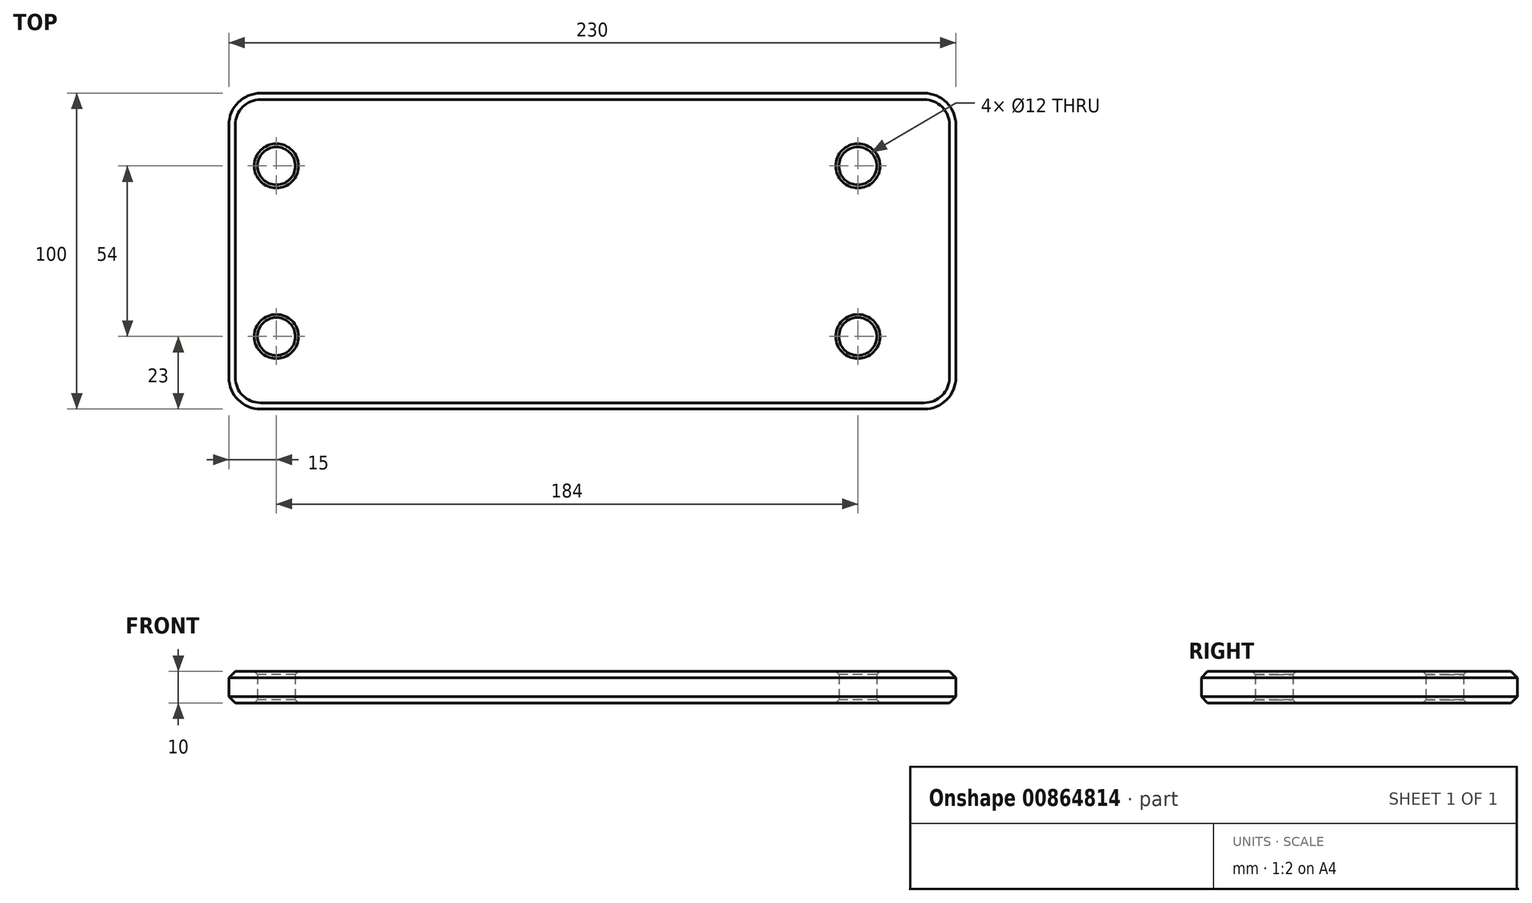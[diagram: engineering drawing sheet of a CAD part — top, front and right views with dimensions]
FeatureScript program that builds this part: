
annotation { "Feature Type Name" : "Feature", "Feature Type Description" : "" }
export const myFeature = defineFeature(function(context is Context, id is Id, definition is map)
    precondition{}
    {
        {
            var Q0;
            Q0=qCreatedBy(makeId("Top.planeOp"),FACE);
            var sketch = newSketch(context, id + "F0", { "sketchPlane" : qUnion([Q0])});
            skLineSegment(sketch, "E0.bottom", {"start": v(105, 50) * mm, "end": v(-105, 50) * mm});
            skLineSegment(sketch, "E0.top", {"start": v(105, -50) * mm, "end": v(-105, -50) * mm});
            skLineSegment(sketch, "E0.left", {"start": v(115, 40) * mm, "end": v(115, -40) * mm});
            skLineSegment(sketch, "E0.right", {"start": v(-115, 40) * mm, "end": v(-115, -40) * mm});
            skPoint(sketch, "E0.middle", {"position": v(0, 0) * mm});
            skPoint(sketch, "E1.visualSharp", {"position": v(-115, 50) * mm});
            skArc(sketch, "E1.filletArc", {"start": v(-105, 50) * mm, "mid": v(-112.07, 47.07) * mm, "end": v(-115, 40) * mm});
            skPoint(sketch, "E2.visualSharp", {"position": v(-115, -50) * mm});
            skArc(sketch, "E2.filletArc", {"start": v(-115, -40) * mm, "mid": v(-112.07, -47.07) * mm, "end": v(-105, -50) * mm});
            skPoint(sketch, "E3.visualSharp", {"position": v(115, 50) * mm});
            skArc(sketch, "E3.filletArc", {"start": v(115, 40) * mm, "mid": v(112.07, 47.07) * mm, "end": v(105, 50) * mm});
            skPoint(sketch, "E4.visualSharp", {"position": v(115, -50) * mm});
            skArc(sketch, "E4.filletArc", {"start": v(105, -50) * mm, "mid": v(112.07, -47.07) * mm, "end": v(115, -40) * mm});
            skLineSegment(sketch, "E5", {"start": v(-100, 50) * mm, "end": v(-100, -50) * mm, "construction": true});
            skLineSegment(sketch, "E6", {"start": v(-115, -27) * mm, "end": v(115, -27) * mm, "construction": true});
            skLineSegment(sketch, "E7", {"start": v(-115, 27) * mm, "end": v(115, 27) * mm, "construction": true});
            skLineSegment(sketch, "E8", {"start": v(84, 50) * mm, "end": v(84, -50) * mm, "construction": true});
            skCircle(sketch, "E9", {"center": v(-100, 27) * mm, "radius": 6 * mm});
            skCircle(sketch, "E10", {"center": v(-100, -27) * mm, "radius": 6 * mm});
            skCircle(sketch, "E11", {"center": v(84, 27) * mm, "radius": 6 * mm});
            skCircle(sketch, "E12", {"center": v(84, -27) * mm, "radius": 6 * mm});
            skSolve(sketch);
        }
        {
            var Q0;
            Q0=makeQuery(id+"F0.imprint","IMPRINT",FACE,{"disambiguationData":[TD([[makeQuery(id+"F0.imprint","IMPRINT",EDGE,{"derivedFrom":sQuery(id+"F0.wireOp",EDGE,"E0.bottom")}),1.0]])]});
            extrude(context, id + "F1", {"entities" : qUnion([Q0]), "depth" : 10 * mm, "offsetDistance" : 25 * mm});
        }
        {
            var Q0;
            Q0=makeQuery(id+"F1.opExtrude","CAP_EDGE",EDGE,{"disambiguationData":[OSD([sQuery(id+"F0.wireOp",EDGE,"E0.top")])],"isStart":false});
            chamfer(context, id + "F2", {"entities" : qUnion([Q0]), "width" : 2 * mm, "tangentPropagation" : true});
        }
        {
            var Q0;
            Q0=makeQuery(id+"F1.opExtrude","CAP_EDGE",EDGE,{"disambiguationData":[OSD([sQuery(id+"F0.wireOp",EDGE,"E0.top")])],"isStart":true});
            chamfer(context, id + "F3", {"entities" : qUnion([Q0]), "width" : 2 * mm, "tangentPropagation" : true});
        }
        {
            var Q0;
            Q0=makeQuery(id+"F1.opExtrude","CAP_EDGE",EDGE,{"disambiguationData":[OSD([sQuery(id+"F0.wireOp",EDGE,"E10")])],"isStart":false});
            var Q1;
            Q1=makeQuery(id+"F1.opExtrude","CAP_EDGE",EDGE,{"disambiguationData":[OSD([sQuery(id+"F0.wireOp",EDGE,"E9")])],"isStart":false});
            var Q2;
            Q2=makeQuery(id+"F1.opExtrude","CAP_EDGE",EDGE,{"disambiguationData":[OSD([sQuery(id+"F0.wireOp",EDGE,"E11")])],"isStart":false});
            var Q3;
            Q3=makeQuery(id+"F1.opExtrude","CAP_EDGE",EDGE,{"disambiguationData":[OSD([sQuery(id+"F0.wireOp",EDGE,"E12")])],"isStart":false});
            chamfer(context, id + "F4", {"entities" : qUnion([Q0, Q1, Q2, Q3]), "width" : 1 * mm, "tangentPropagation" : true});
        }
        {
            var Q0;
            Q0=makeQuery(id+"F1.opExtrude","CAP_EDGE",EDGE,{"disambiguationData":[OSD([sQuery(id+"F0.wireOp",EDGE,"E12")])],"isStart":true});
            var Q1;
            Q1=makeQuery(id+"F1.opExtrude","CAP_EDGE",EDGE,{"disambiguationData":[OSD([sQuery(id+"F0.wireOp",EDGE,"E11")])],"isStart":true});
            var Q2;
            Q2=makeQuery(id+"F1.opExtrude","CAP_EDGE",EDGE,{"disambiguationData":[OSD([sQuery(id+"F0.wireOp",EDGE,"E10")])],"isStart":true});
            var Q3;
            Q3=makeQuery(id+"F1.opExtrude","CAP_EDGE",EDGE,{"disambiguationData":[OSD([sQuery(id+"F0.wireOp",EDGE,"E9")])],"isStart":true});
            chamfer(context, id + "F5", {"entities" : qUnion([Q0, Q1, Q2, Q3]), "width" : 1 * mm, "tangentPropagation" : true});
        }
    });
